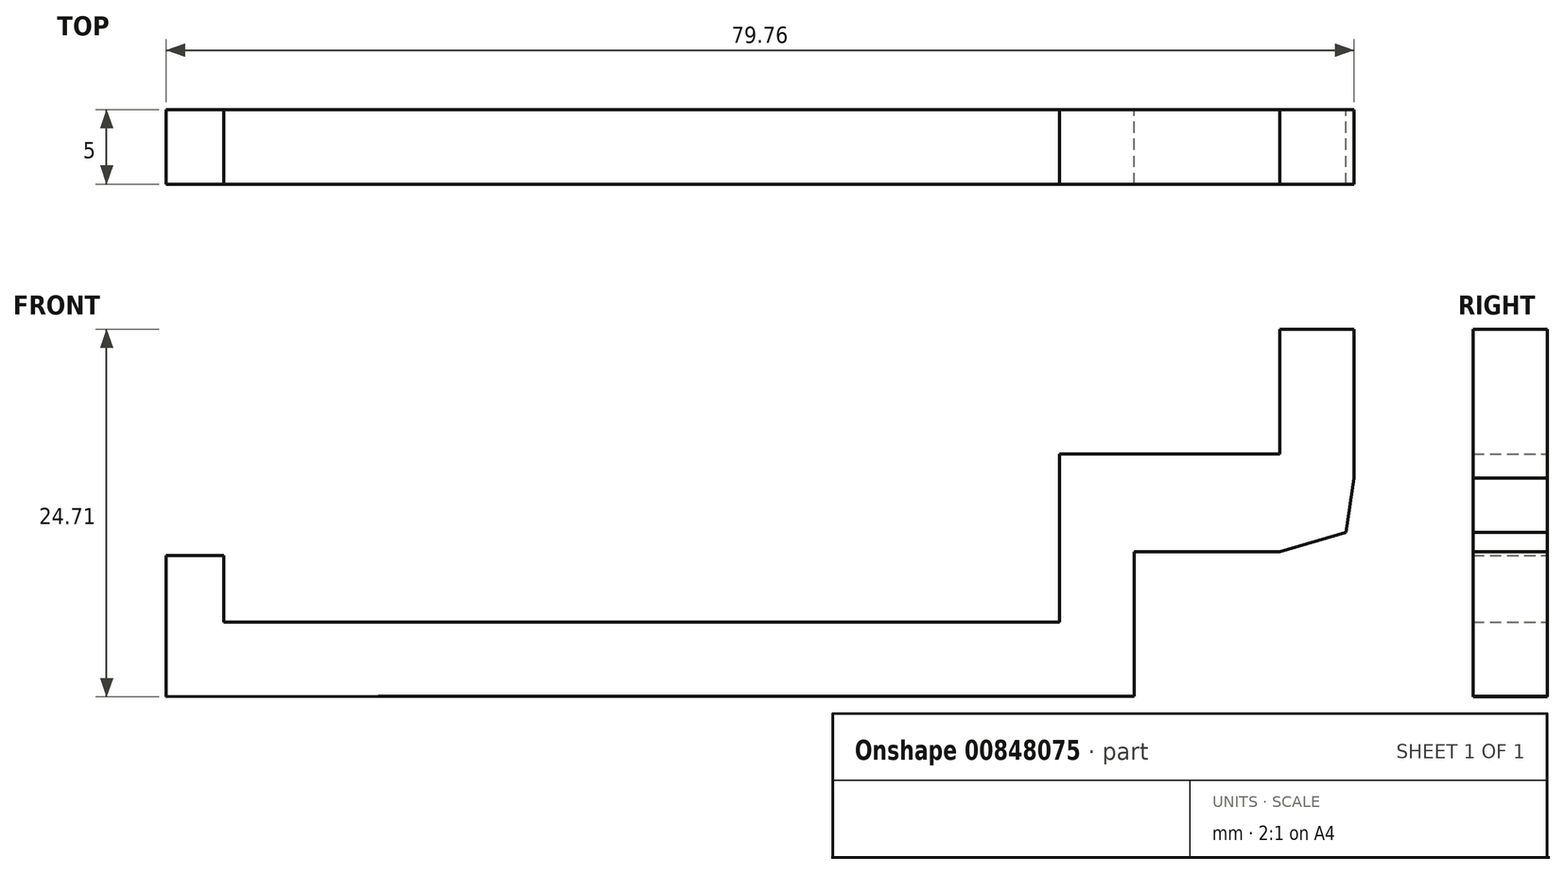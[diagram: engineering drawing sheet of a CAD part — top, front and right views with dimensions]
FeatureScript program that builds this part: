
annotation { "Feature Type Name" : "Feature", "Feature Type Description" : "" }
export const myFeature = defineFeature(function(context is Context, id is Id, definition is map)
    precondition{}
    {
        {
            var Q0;
            Q0=qCreatedBy(makeId("Front.planeOp"),FACE);
            var sketch = newSketch(context, id + "F0", { "sketchPlane" : qUnion([Q0])});
            skLineSegment(sketch, "E0", {"start": v(-13.3, -12.35) * mm, "end": v(37.47, -12.35) * mm});
            skLineSegment(sketch, "E1", {"start": v(37.47, -12.35) * mm, "end": v(37.47, -2.64) * mm});
            skLineSegment(sketch, "E2", {"start": v(37.47, -2.64) * mm, "end": v(47.26, -2.64) * mm});
            skLineSegment(sketch, "E3", {"start": v(47.26, -2.64) * mm, "end": v(51.72, -1.34) * mm});
            skLineSegment(sketch, "E4", {"start": v(51.72, -1.34) * mm, "end": v(52.23, 2.3) * mm});
            skLineSegment(sketch, "E5", {"start": v(52.23, 2.3) * mm, "end": v(52.23, 12.32) * mm});
            skLineSegment(sketch, "E6", {"start": v(52.23, 12.32) * mm, "end": v(47.26, 12.32) * mm});
            skLineSegment(sketch, "E7", {"start": v(47.26, 12.32) * mm, "end": v(47.26, 3.94) * mm});
            skLineSegment(sketch, "E8", {"start": v(47.26, 3.94) * mm, "end": v(32.47, 3.94) * mm});
            skLineSegment(sketch, "E9", {"start": v(32.47, 3.94) * mm, "end": v(32.47, -7.4) * mm});
            skLineSegment(sketch, "E10", {"start": v(32.47, -7.4) * mm, "end": v(-10.14, -7.4) * mm});
            skLineSegment(sketch, "E11", {"start": v(-10.14, -7.4) * mm, "end": v(-27.53, -7.4) * mm});
            skLineSegment(sketch, "E12", {"start": v(-27.53, -7.4) * mm, "end": v(-27.53, -12.4) * mm});
            skLineSegment(sketch, "E13", {"start": v(-27.53, -12.4) * mm, "end": v(-13.3, -12.35) * mm});
            skLineSegment(sketch, "E14", {"start": v(-27.53, -7.4) * mm, "end": v(-27.53, -2.9) * mm});
            skLineSegment(sketch, "E15", {"start": v(-27.53, -2.9) * mm, "end": v(-23.66, -2.9) * mm});
            skLineSegment(sketch, "E16", {"start": v(-23.66, -2.9) * mm, "end": v(-23.66, -7.4) * mm});
            skSolve(sketch);
        }
        {
            var Q0;
            Q0 = qSketchRegion(id + "F0", true);
            extrude(context, id + "F1", {"entities" : qUnion([Q0]), "depth" : 5 * mm, "offsetDistance" : 25 * mm});
        }
    });
